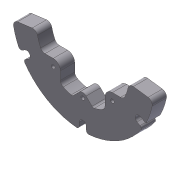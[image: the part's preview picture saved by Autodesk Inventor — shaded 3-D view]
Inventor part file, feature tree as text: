
AUTODESK INVENTOR PART (.ipt)
format: ipt  version: 2012 (Build 160160000, 160)  size: 166,912 bytes
history: native  units: in
note: dims shown in document units (in); Inventor stores cm internally (conversion verified against a paired STEP export)
features: extrude x1, sketch x1
ambient origin geometry x8: Origin, YZ Plane, XZ Plane, XY Plane, X Axis, Y Axis, Z Axis, Center Point
feature tree (2):
  extrude  "Extrusion3"  Depth=0.375in
  sketch  "Sketch1"  dims[d2=165.0deg d5=0.375in d7=4.375in d8=0.192in d9=3.7in d10=0.1875in d11=60.0deg d12=0.3125in d13=60.0deg d16=0.25in d17=0.125in d18=0.25in d19=0.125in d20=0.75in d21=0.0in]
